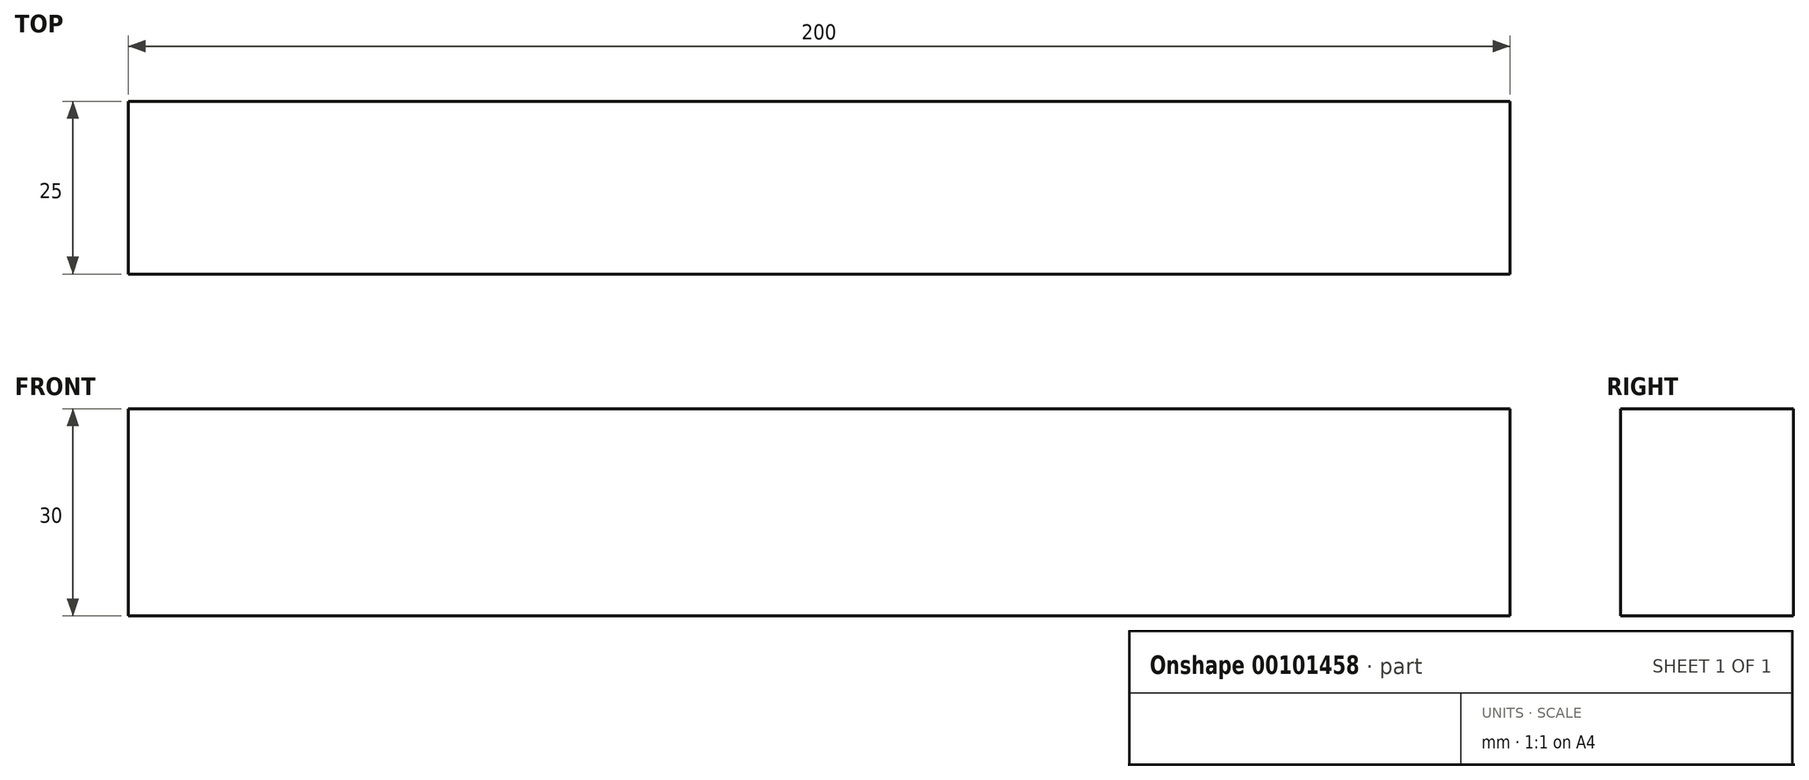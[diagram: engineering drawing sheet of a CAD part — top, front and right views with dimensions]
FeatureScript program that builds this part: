
annotation { "Feature Type Name" : "Feature", "Feature Type Description" : "" }
export const myFeature = defineFeature(function(context is Context, id is Id, definition is map)
    precondition{}
    {
        {
            var Q0;
            Q0=qCreatedBy(makeId("Front.planeOp"),FACE);
            var sketch = newSketch(context, id + "F0", { "sketchPlane" : qUnion([Q0])});
            skLineSegment(sketch, "E0.bottom", {"start": v(0, 15) * mm, "end": v(200, 15) * mm});
            skLineSegment(sketch, "E0.top", {"start": v(0, -15) * mm, "end": v(200, -15) * mm});
            skLineSegment(sketch, "E0.left", {"start": v(0, 15) * mm, "end": v(0, -15) * mm});
            skLineSegment(sketch, "E0.right", {"start": v(200, 15) * mm, "end": v(200, -15) * mm});
            skSolve(sketch);
        }
        {
            var Q0;
            Q0=makeQuery(id+"F0.imprint","IMPRINT",FACE,{"disambiguationData":[TD([[makeQuery(id+"F0.imprint","IMPRINT",EDGE,{"derivedFrom":sQuery(id+"F0.wireOp",EDGE,"E0.bottom")}),-1.0]])]});
            extrude(context, id + "F1", {"entities" : qUnion([Q0]), "depth" : 25 * mm});
        }
    });
